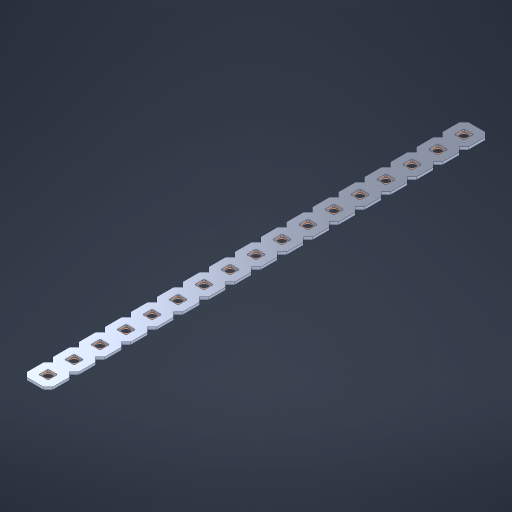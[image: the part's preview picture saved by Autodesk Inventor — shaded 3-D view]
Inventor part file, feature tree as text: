
AUTODESK INVENTOR PART (.ipt)
format: ipt  version: 2023 (Build 270158000, 158)  size: 478,720 bytes
history: native  units: in
note: dims shown in document units (in); Inventor stores cm internally (conversion verified against a paired STEP export)
features: other x18, extrude x16, sketch x2, pattern_linear x1
ambient origin geometry x8: Origin, YZ Plane, XZ Plane, XY Plane, X Axis, Y Axis, Z Axis, Center Point
bodies: Solid1 (feature_tree), Body (feature_tree)
feature tree (37):
  pattern_linear  "Rectangular Pattern1"  Spacing1=0.09in  [1 undecoded]
  sketch  "Sketch1"  dims[d1=0.5in]
  sketch  "Sketch2"  dims[d2=0.182in d3=0.09in d4=0.09in d5=0.09in d6=0.09in d7=0.09in d8=0.09in d9=0.09in d10=0.09in d11=0.02in d13=0.0in d14=0.172in d15=0.0625in d16=0.0in d19=0.5in d22=0.5in]
  other  "Srf1"
  other  "Srf126"
  other  "Srf127"
  other  "Srf128"
  other  "Srf129"
  other  "Srf130"
  other  "Srf131"
  other  "Srf250"
  other  "Srf251"
  other  "Srf252"
  other  "Srf253"
  other  "Srf254"
  other  "Srf255"
  other  "Srf256"
  other  "Srf257"
  other  "Srf258"
  other  "Srf259"
  other  "Circle"
  extrude  "ExtrusionSrf126"  Depth=0.09in
  extrude  "ExtrusionSrf127"  Depth=0.09in
  extrude  "ExtrusionSrf128"  Depth=0.09in
  extrude  "ExtrusionSrf129"  Depth=0.09in
  extrude  "ExtrusionSrf130"  Depth=0.09in
  extrude  "ExtrusionSrf131"  Depth=0.09in
  extrude  "ExtrusionSrf250"  Depth=0.09in
  extrude  "ExtrusionSrf251"  Depth=0.02in
  extrude  "ExtrusionSrf252"  TaperAngle=0.0deg  [1 undecoded]
  extrude  "ExtrusionSrf253"  Depth=0.5in
  extrude  "ExtrusionSrf254"  Depth=0.5in TaperAngle=0.0deg
  extrude  "ExtrusionSrf255"  Depth=0.5in
  extrude  "ExtrusionSrf256"  Depth=0.5in
  extrude  "ExtrusionSrf257"  [1 undecoded]
  extrude  "ExtrusionSrf258"  [1 undecoded]
  extrude  "ExtrusionSrf259"  [1 undecoded]
note: 5 required parameter values undecoded (feature->parameter linkage not recoverable at this tier; creation-order binding heuristic only, values carry confidence <= 0.55)
